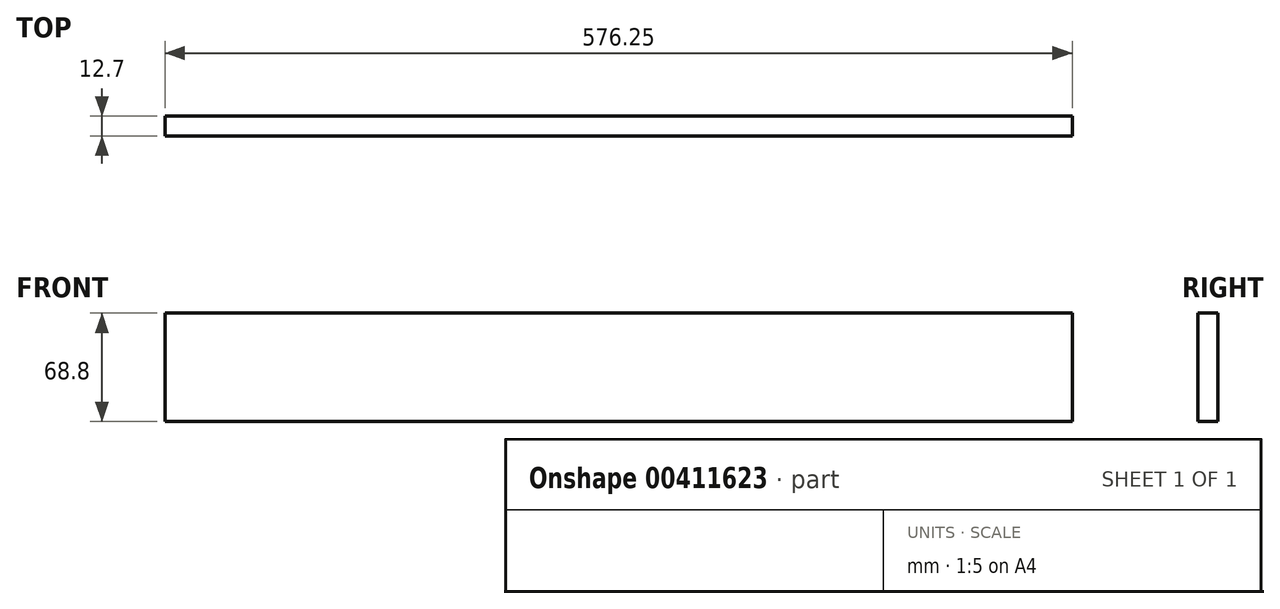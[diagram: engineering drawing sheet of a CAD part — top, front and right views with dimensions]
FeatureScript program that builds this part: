
annotation { "Feature Type Name" : "Feature", "Feature Type Description" : "" }
export const myFeature = defineFeature(function(context is Context, id is Id, definition is map)
    precondition{}
    {
        {
            var Q0;
            Q0=qCreatedBy(makeId("Front.planeOp"),FACE);
            var sketch = newSketch(context, id + "F0", { "sketchPlane" : qUnion([Q0])});
            skLineSegment(sketch, "E0.bottom", {"start": v(417.12, -44) * mm, "end": v(-159.13, -44) * mm});
            skLineSegment(sketch, "E0.top", {"start": v(417.12, -112.8) * mm, "end": v(-159.13, -112.8) * mm});
            skLineSegment(sketch, "E0.left", {"start": v(417.12, -44) * mm, "end": v(417.12, -112.8) * mm});
            skLineSegment(sketch, "E0.right", {"start": v(-159.13, -44) * mm, "end": v(-159.13, -112.8) * mm});
            skSolve(sketch);
        }
        {
            var Q0;
            Q0=makeQuery(id+"F0.imprint","IMPRINT",FACE,{"disambiguationData":[TD([[makeQuery(id+"F0.imprint","IMPRINT",EDGE,{"derivedFrom":sQuery(id+"F0.wireOp",EDGE,"E0.bottom")}),1.0]])]});
            extrude(context, id + "F1", {"entities" : qUnion([Q0]), "depth" : 12.7 * mm});
        }
    });
